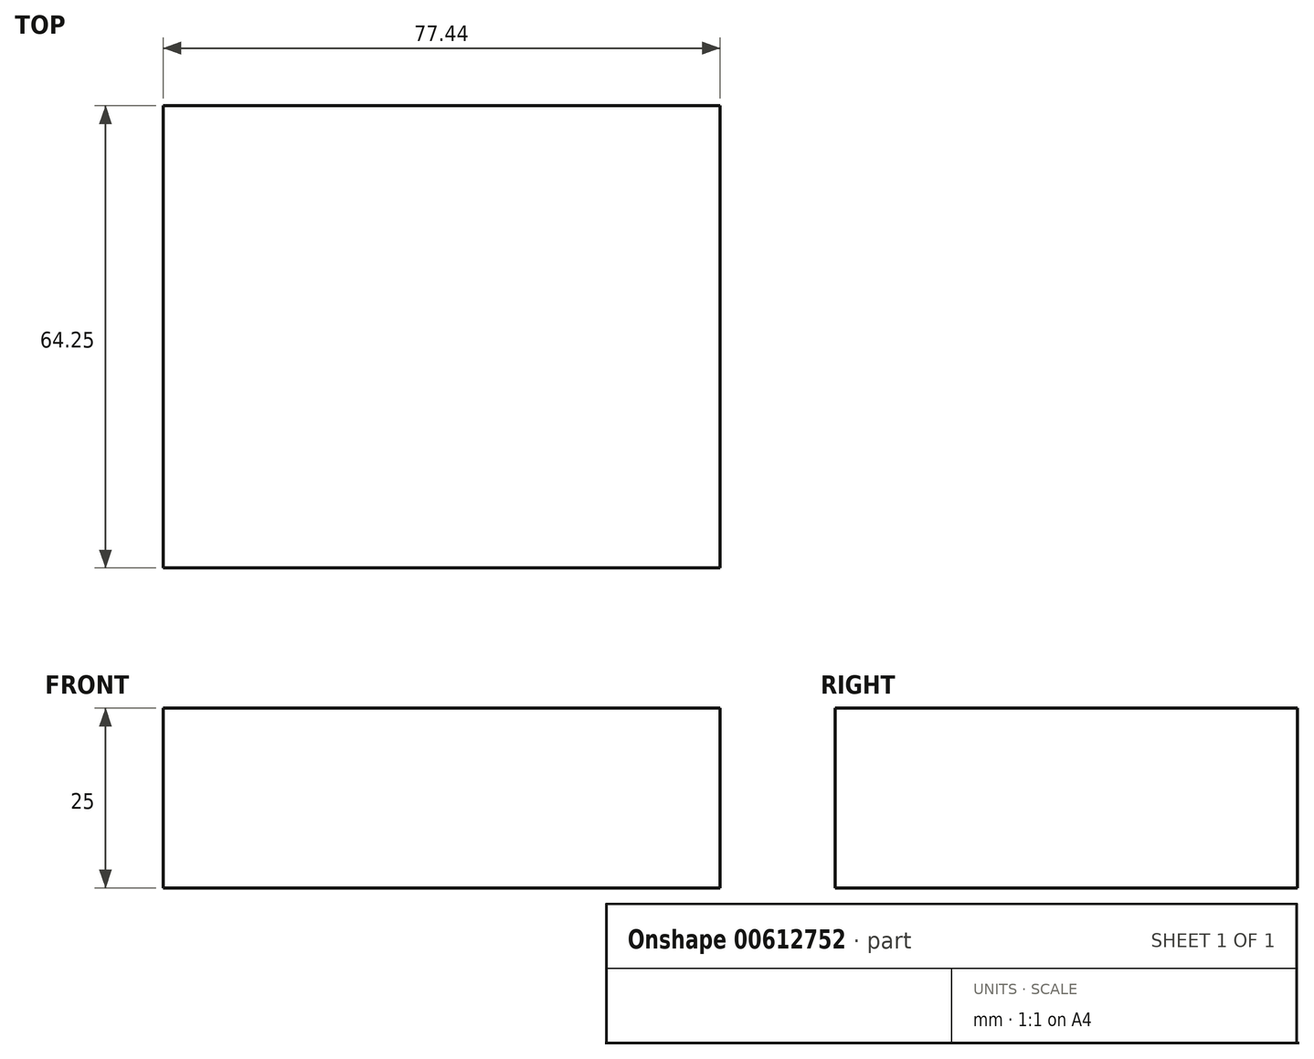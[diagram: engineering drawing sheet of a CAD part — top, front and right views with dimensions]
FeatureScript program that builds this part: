
annotation { "Feature Type Name" : "Feature", "Feature Type Description" : "" }
export const myFeature = defineFeature(function(context is Context, id is Id, definition is map)
    precondition{}
    {
        {
            var Q0;
            Q0=qCreatedBy(makeId("Top.planeOp"),FACE);
            var sketch = newSketch(context, id + "F0", { "sketchPlane" : qUnion([Q0])});
            skLineSegment(sketch, "E0.bottom", {"start": v(-38.53, 26.03) * mm, "end": v(38.91, 26.03) * mm});
            skLineSegment(sketch, "E0.top", {"start": v(-38.53, -38.22) * mm, "end": v(38.91, -38.22) * mm});
            skLineSegment(sketch, "E0.left", {"start": v(-38.53, 26.03) * mm, "end": v(-38.53, -38.22) * mm});
            skLineSegment(sketch, "E0.right", {"start": v(38.91, 26.03) * mm, "end": v(38.91, -38.22) * mm});
            skSolve(sketch);
        }
        {
            var Q0;
            Q0=makeQuery(id+"F0.imprint","IMPRINT",FACE,{"disambiguationData":[TD([[makeQuery(id+"F0.imprint","IMPRINT",EDGE,{"derivedFrom":sQuery(id+"F0.wireOp",EDGE,"E0.bottom")}),-1.0]])]});
            extrude(context, id + "F1", {"entities" : qUnion([Q0]), "depth" : 25 * mm, "offsetDistance" : 25 * mm});
        }
    });
